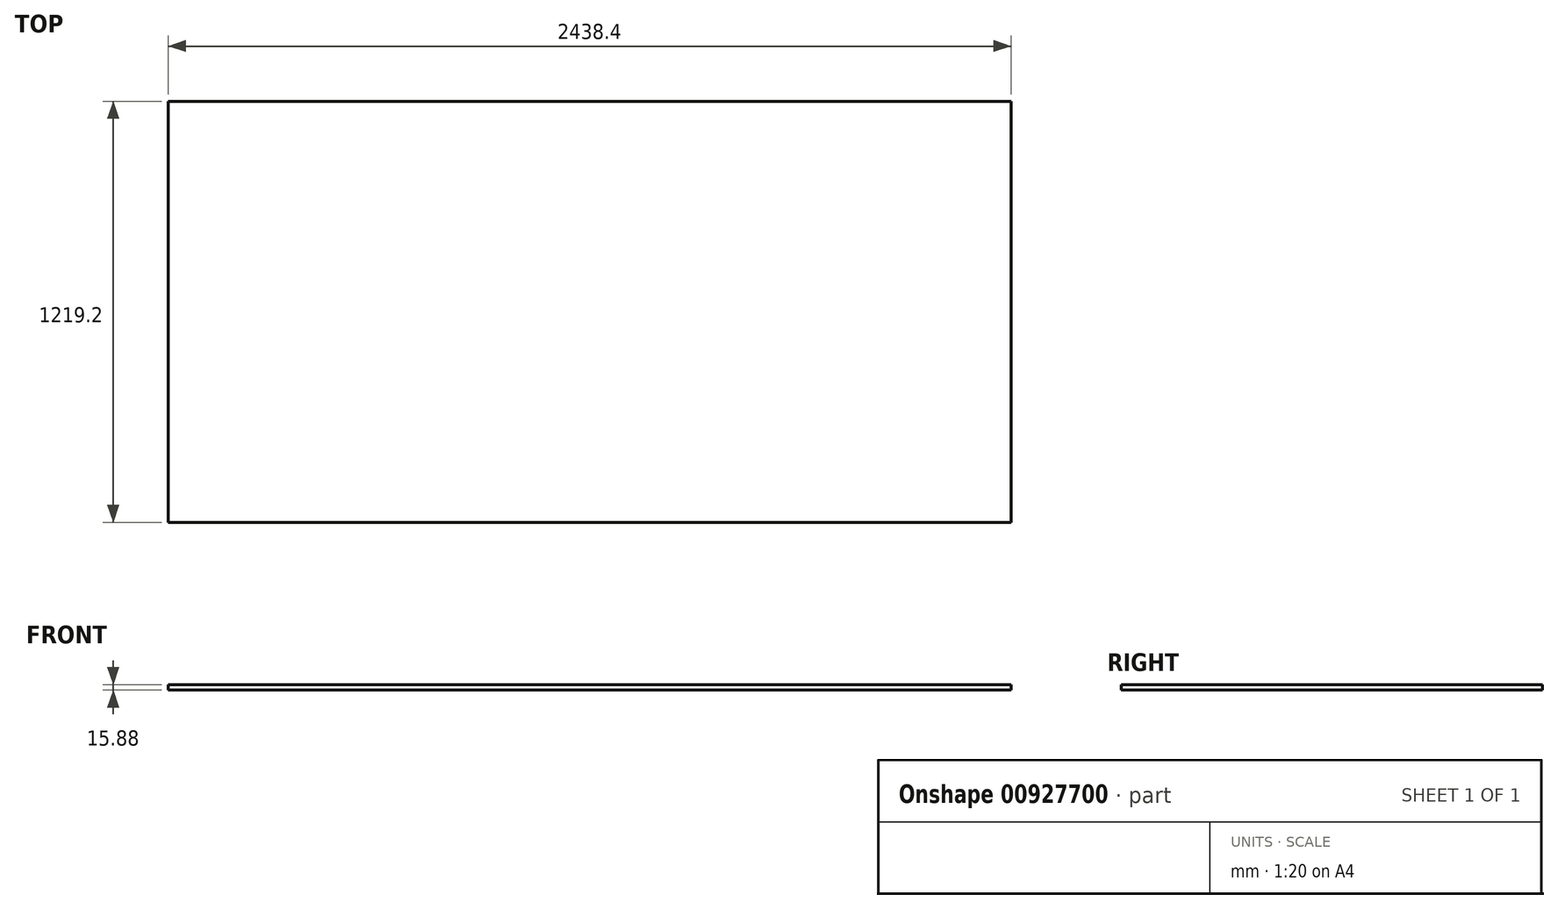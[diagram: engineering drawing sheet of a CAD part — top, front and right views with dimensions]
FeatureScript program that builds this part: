
annotation { "Feature Type Name" : "Feature", "Feature Type Description" : "" }
export const myFeature = defineFeature(function(context is Context, id is Id, definition is map)
    precondition{}
    {
        {
            var Q0;
            Q0=qCreatedBy(makeId("Top.planeOp"),FACE);
            var sketch = newSketch(context, id + "F0", { "sketchPlane" : qUnion([Q0])});
            skLineSegment(sketch, "E0.bottom", {"start": v(-1257.07, 770.8) * mm, "end": v(1181.33, 770.8) * mm});
            skLineSegment(sketch, "E0.top", {"start": v(-1257.07, -448.4) * mm, "end": v(1181.33, -448.4) * mm});
            skLineSegment(sketch, "E0.left", {"start": v(-1257.07, 770.8) * mm, "end": v(-1257.07, -448.4) * mm});
            skLineSegment(sketch, "E0.right", {"start": v(1181.33, 770.8) * mm, "end": v(1181.33, -448.4) * mm});
            skSolve(sketch);
        }
        {
            var Q0;
            Q0 = qSketchRegion(id + "F0", true);
            extrude(context, id + "F1", {"entities" : qUnion([Q0]), "depth" : 15.88 * mm, "offsetDistance" : 25.4 * mm});
        }
    });
